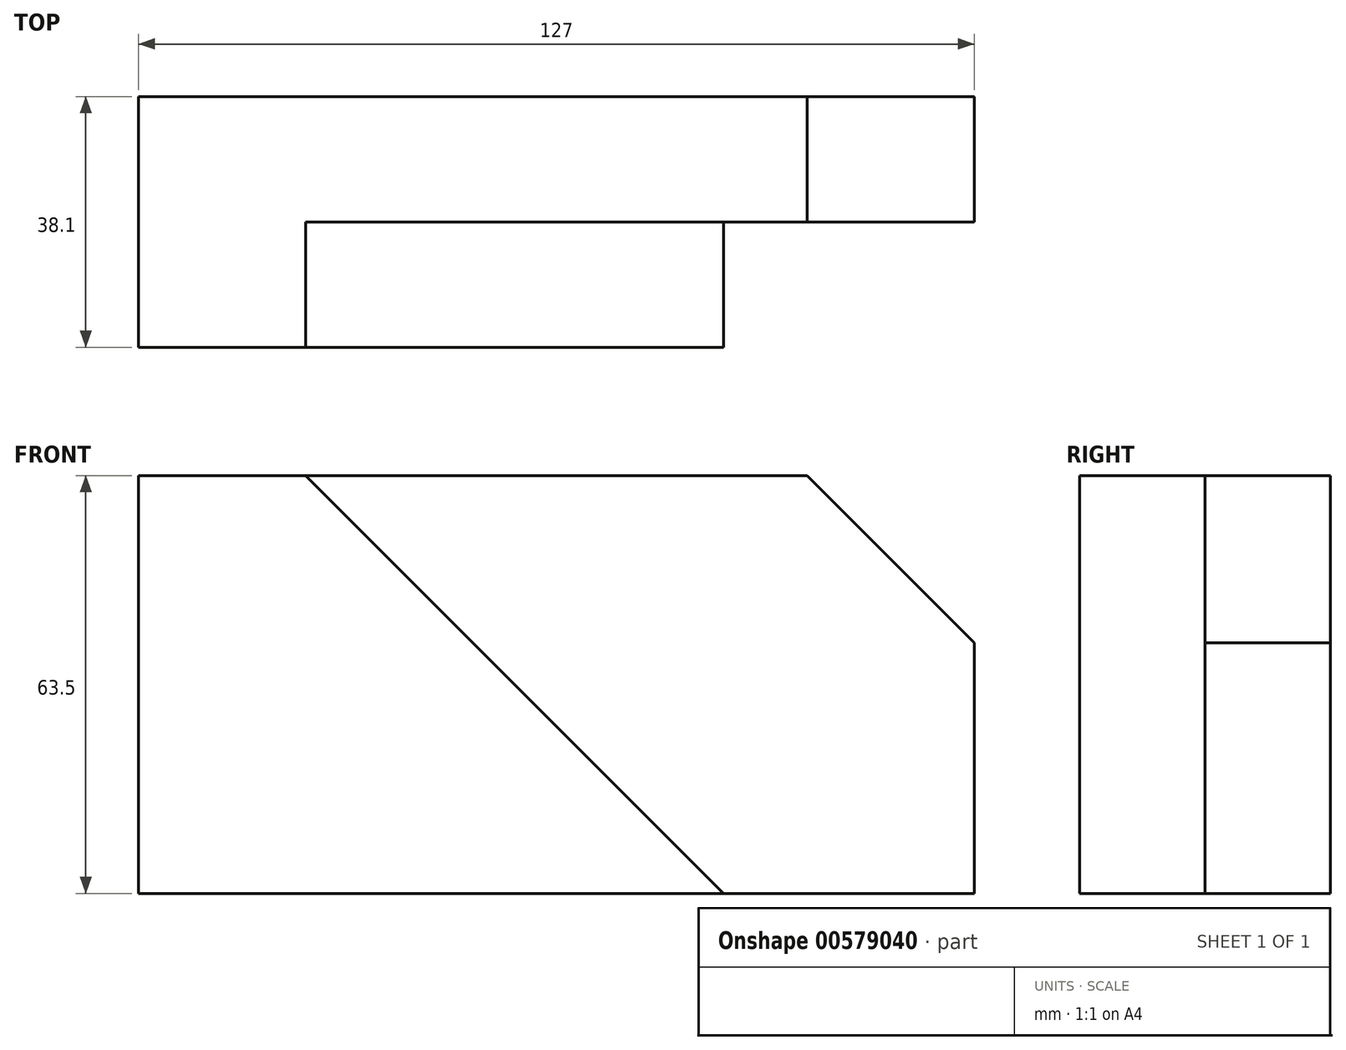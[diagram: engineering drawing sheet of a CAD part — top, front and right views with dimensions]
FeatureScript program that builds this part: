
annotation { "Feature Type Name" : "Feature", "Feature Type Description" : "" }
export const myFeature = defineFeature(function(context is Context, id is Id, definition is map)
    precondition{}
    {
        {
            var Q0;
            Q0=qCreatedBy(makeId("Front.planeOp"),FACE);
            var sketch = newSketch(context, id + "F0", { "sketchPlane" : qUnion([Q0])});
            skLineSegment(sketch, "E0", {"start": v(-48.68, 25.4) * mm, "end": v(-48.68, -38.1) * mm});
            skLineSegment(sketch, "E1", {"start": v(-48.68, -38.1) * mm, "end": v(78.32, -38.1) * mm});
            skLineSegment(sketch, "E2", {"start": v(78.32, -38.1) * mm, "end": v(78.32, 0) * mm});
            skLineSegment(sketch, "E3", {"start": v(-48.68, 25.4) * mm, "end": v(52.92, 25.4) * mm});
            skLineSegment(sketch, "E4", {"start": v(52.92, 25.4) * mm, "end": v(78.32, 0) * mm});
            skLineSegment(sketch, "E5", {"start": v(-48.68, 25.4) * mm, "end": v(-23.28, 25.4) * mm});
            skLineSegment(sketch, "E6", {"start": v(-48.68, -38.1) * mm, "end": v(40.22, -38.1) * mm});
            skLineSegment(sketch, "E7", {"start": v(-23.28, 25.4) * mm, "end": v(40.22, -38.1) * mm});
            skSolve(sketch);
        }
        {
            var Q0;
            Q0 = qSketchRegion(id + "F0", true);
            extrude(context, id + "F1", {"entities" : qUnion([Q0]), "depth" : 38.1 * mm, "offsetDistance" : 25.4 * mm});
        }
        {
            var Q0;
            Q0=makeQuery(id+"F1.opExtrude","CAP_FACE",FACE,{"disambiguationData":[OSD([sQuery(id+"F0.wireOp",EDGE,"E0"),sQuery(id+"F0.wireOp",EDGE,"E1"),sQuery(id+"F0.wireOp",EDGE,"E2"),sQuery(id+"F0.wireOp",EDGE,"E3"),sQuery(id+"F0.wireOp",EDGE,"E4"),sQuery(id+"F0.wireOp",EDGE,"E5"),sQuery(id+"F0.wireOp",EDGE,"E6")])],"isStart":false});
            var sketch = newSketch(context, id + "F2", { "sketchPlane" : qUnion([Q0])});
            skLineSegment(sketch, "E8", {"start": v(-48.68, 25.4) * mm, "end": v(-23.28, 25.4) * mm});
            skLineSegment(sketch, "E9", {"start": v(-48.68, -38.1) * mm, "end": v(40.22, -38.1) * mm});
            skLineSegment(sketch, "E10", {"start": v(40.22, -38.1) * mm, "end": v(-23.28, 25.4) * mm});
            skLineSegment(sketch, "E11", {"start": v(40.22, -38.1) * mm, "end": v(78.32, -38.1) * mm});
            skLineSegment(sketch, "E12", {"start": v(78.32, -38.1) * mm, "end": v(78.32, 0) * mm});
            skLineSegment(sketch, "E13", {"start": v(78.32, 0) * mm, "end": v(52.92, 25.4) * mm});
            skLineSegment(sketch, "E14", {"start": v(52.92, 25.4) * mm, "end": v(-23.28, 25.4) * mm});
            skSolve(sketch);
        }
        {
            var Q0;
            Q0 = qSketchRegion(id + "F2", true);
            extrude(context, id + "F3", {"entities" : qUnion([Q0]), "operationType" : NewBodyOperationType.REMOVE, "oppositeDirection" : true, "depth" : 19.05 * mm, "offsetDistance" : 25.4 * mm});
        }
    });
